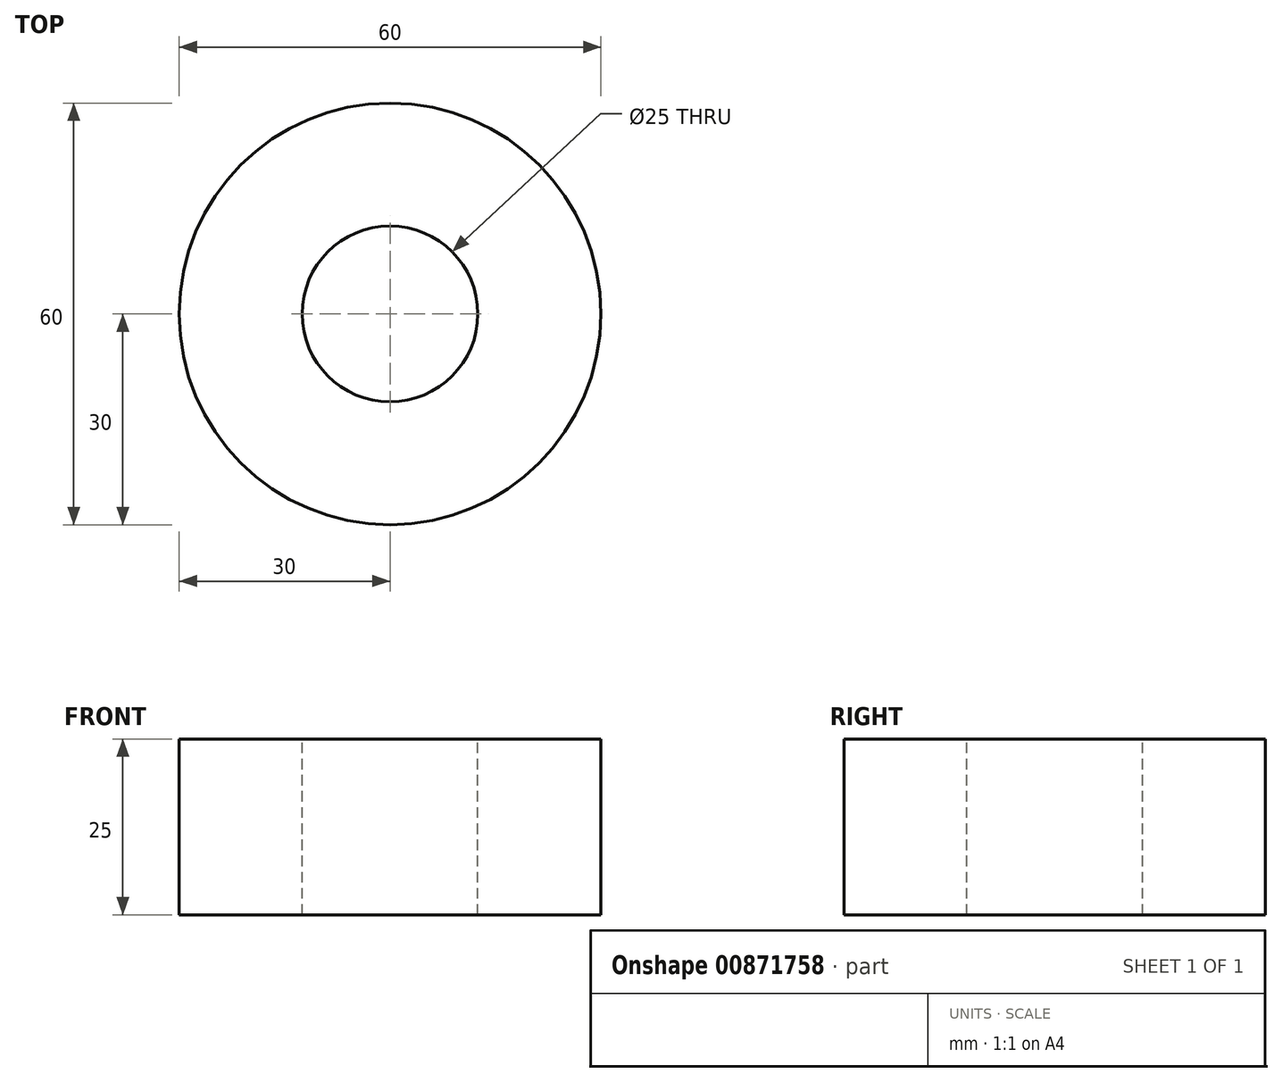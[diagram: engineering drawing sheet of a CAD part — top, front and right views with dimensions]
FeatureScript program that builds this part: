
annotation { "Feature Type Name" : "Feature", "Feature Type Description" : "" }
export const myFeature = defineFeature(function(context is Context, id is Id, definition is map)
    precondition{}
    {
        {
            var Q0;
            Q0=qCreatedBy(makeId("Top.planeOp"),FACE);
            var sketch = newSketch(context, id + "F0", { "sketchPlane" : qUnion([Q0])});
            skCircle(sketch, "E0", {"center": v(0, 0) * mm, "radius": 30 * mm});
            skCircle(sketch, "E1.0", {"center": v(0, 0) * mm, "radius": 12.5 * mm});
            skSolve(sketch);
        }
        {
            var Q0;
            Q0=makeQuery(id+"F0.imprint","IMPRINT",FACE,{"disambiguationData":[TD([[makeQuery(id+"F0.imprint","IMPRINT",EDGE,{"derivedFrom":sQuery(id+"F0.wireOp",EDGE,"E0")}),1.0]])]});
            extrude(context, id + "F1", {"entities" : qUnion([Q0]), "oppositeDirection" : true, "depth" : 25 * mm, "offsetDistance" : 25 * mm});
        }
    });
